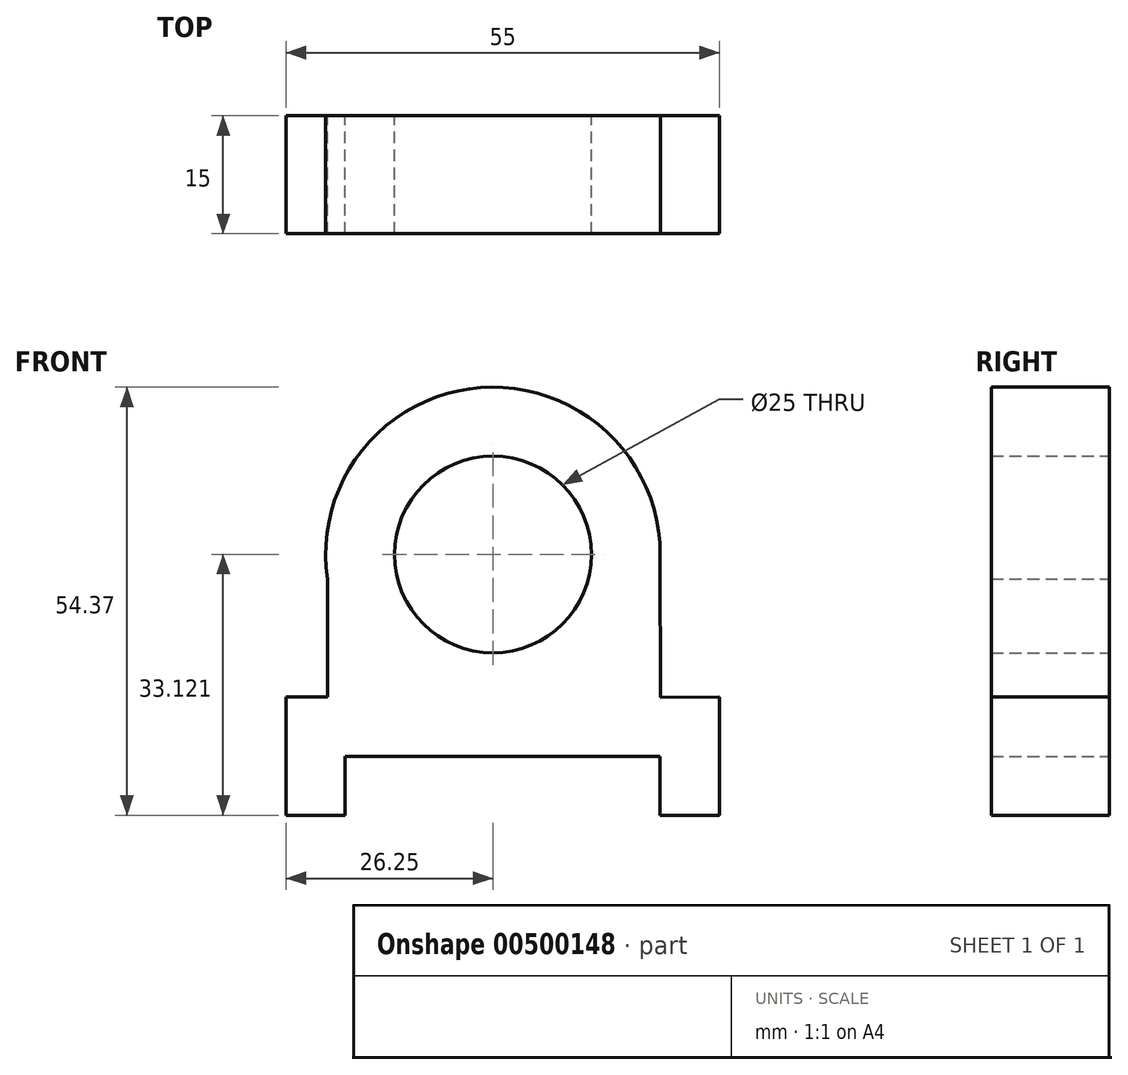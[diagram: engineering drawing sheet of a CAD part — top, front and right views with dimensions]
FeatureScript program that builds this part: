
annotation { "Feature Type Name" : "Feature", "Feature Type Description" : "" }
export const myFeature = defineFeature(function(context is Context, id is Id, definition is map)
    precondition{}
    {
        {
            var Q0;
            Q0=qCreatedBy(makeId("Front.planeOp"),FACE);
            var sketch = newSketch(context, id + "F0", { "sketchPlane" : qUnion([Q0])});
            skLineSegment(sketch, "E0", {"start": v(0, 0) * mm, "end": v(-7.5, 0) * mm});
            skLineSegment(sketch, "E1", {"start": v(-7.5, 0) * mm, "end": v(-7.5, 7.5) * mm});
            skLineSegment(sketch, "E2", {"start": v(-7.5, 7.5) * mm, "end": v(-47.5, 7.5) * mm});
            skLineSegment(sketch, "E3", {"start": v(-47.5, 7.5) * mm, "end": v(-47.5, 0) * mm});
            skLineSegment(sketch, "E4", {"start": v(-47.5, 0) * mm, "end": v(-55, 0) * mm});
            skLineSegment(sketch, "E5", {"start": v(-55, 0) * mm, "end": v(-55, 15) * mm});
            skLineSegment(sketch, "E6", {"start": v(-55, 15) * mm, "end": v(-49.77, 15) * mm});
            skLineSegment(sketch, "E7", {"start": v(-49.77, 15) * mm, "end": v(-49.77, 30) * mm});
            skLineSegment(sketch, "E8", {"start": v(-7.5, 33.16) * mm, "end": v(-7.47, 14.99) * mm});
            skLineSegment(sketch, "E9", {"start": v(-7.47, 14.99) * mm, "end": v(0, 15) * mm});
            skLineSegment(sketch, "E10", {"start": v(0, 15) * mm, "end": v(0, 0) * mm});
            skArc(sketch, "E11", {"start": v(-7.5, 33.16) * mm, "mid": v(-30.33, 54.31) * mm, "end": v(-49.77, 30) * mm});
            skCircle(sketch, "E12", {"center": v(-28.75, 33.12) * mm, "radius": 12.5 * mm});
            skSolve(sketch);
        }
        {
            var Q0;
            Q0=makeQuery(id+"F0.imprint","IMPRINT",FACE,{"disambiguationData":[TD([[makeQuery(id+"F0.imprint","IMPRINT",EDGE,{"derivedFrom":sQuery(id+"F0.wireOp",EDGE,"E0")}),-1.0]])]});
            extrude(context, id + "F1", {"entities" : qUnion([Q0]), "depth" : 15 * mm});
        }
    });
